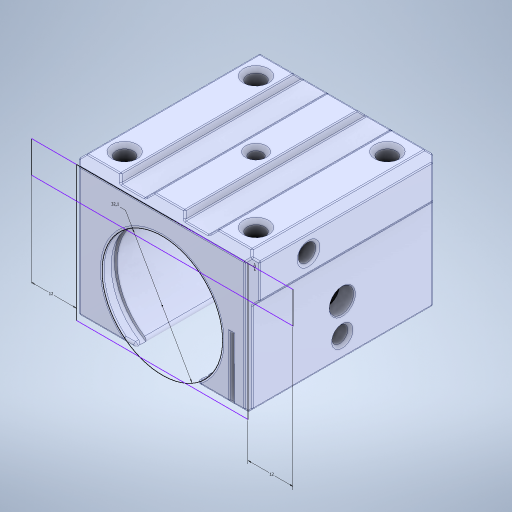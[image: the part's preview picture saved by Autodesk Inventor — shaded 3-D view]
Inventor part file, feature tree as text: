
AUTODESK INVENTOR PART (.ipt)
format: ipt  version: 2024 (Build 280153000, 153)  size: 595,968 bytes
history: native  units: in
note: dims shown in document units (in); Inventor stores cm internally (conversion verified against a paired STEP export)
features: sketch x1, other x1
ambient origin geometry x8: Origin, YZ Plane, XZ Plane, XY Plane, X Axis, Y Axis, Z Axis, Center Point
bodies: Solid3 (feature_tree)
feature tree (2):
  sketch  "Sketch2"  dims[d3=0.0in d4=1.2638in d5=0.4724in d6=0.4724in]
  other  "Корпус SBR20UU_1:3"
